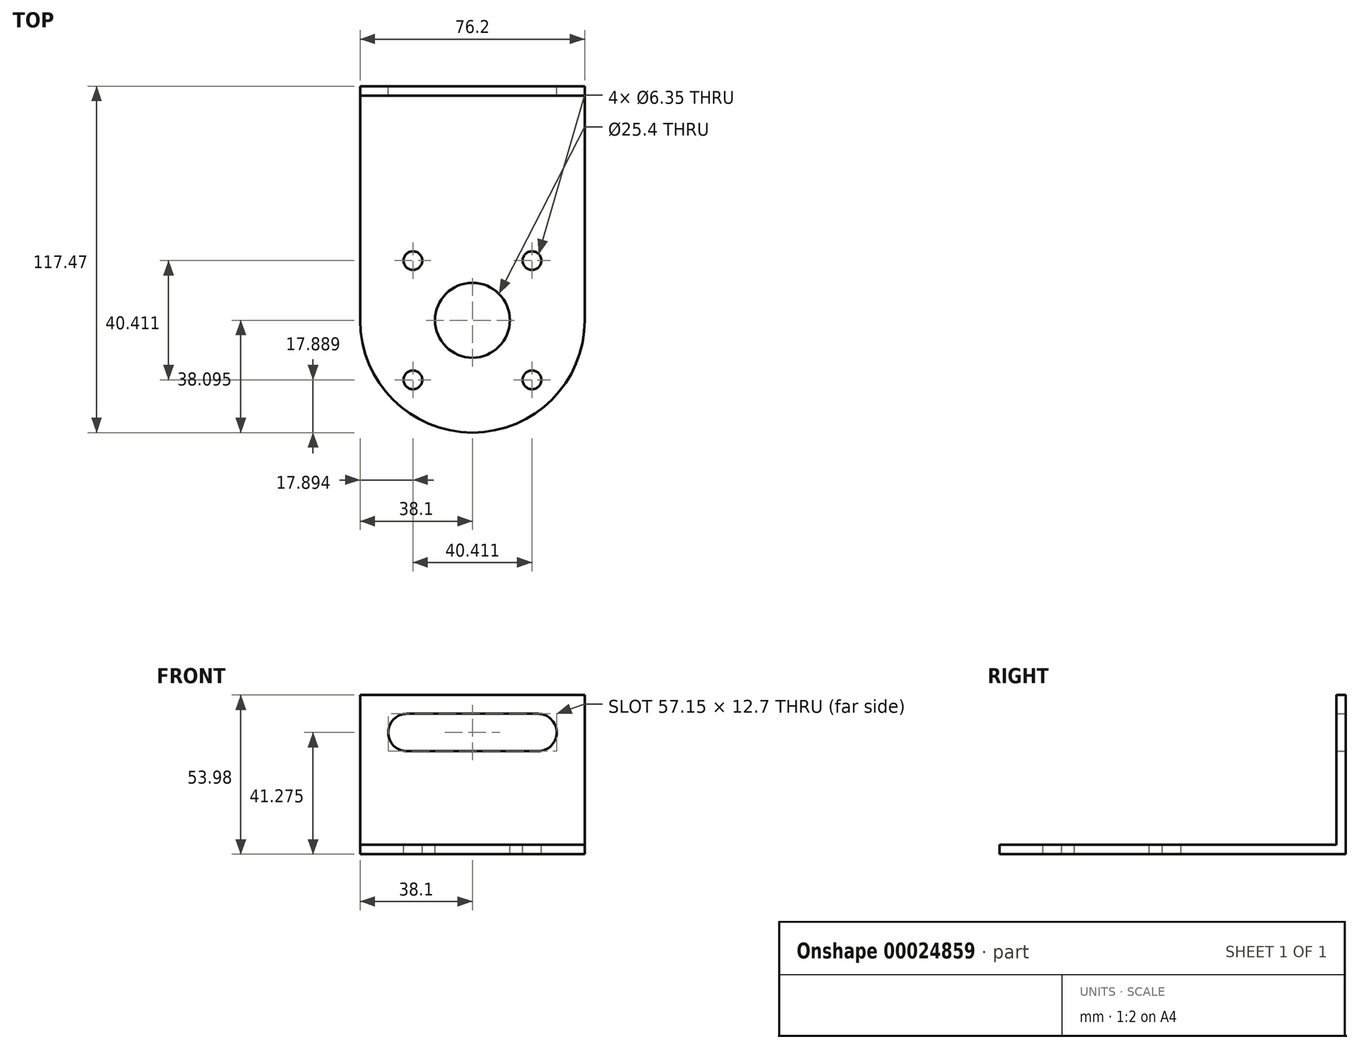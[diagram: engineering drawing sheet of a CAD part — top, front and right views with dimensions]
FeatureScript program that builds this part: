
annotation { "Feature Type Name" : "Feature", "Feature Type Description" : "" }
export const myFeature = defineFeature(function(context is Context, id is Id, definition is map)
    precondition{}
    {
        {
            var Q0;
            Q0=qCreatedBy(makeId("Front.planeOp"),FACE);
            var sketch = newSketch(context, id + "F0", { "sketchPlane" : qUnion([Q0])});
            skLineSegment(sketch, "E0.bottom", {"start": v(0, 0) * mm, "end": v(76.2, 0) * mm});
            skLineSegment(sketch, "E0.top", {"start": v(0, 53.97) * mm, "end": v(76.2, 53.97) * mm});
            skLineSegment(sketch, "E0.left", {"start": v(0, 0) * mm, "end": v(0, 53.97) * mm});
            skLineSegment(sketch, "E0.right", {"start": v(76.2, 0) * mm, "end": v(76.2, 53.97) * mm});
            skLineSegment(sketch, "E1", {"start": v(0, 41.27) * mm, "end": v(76.2, 41.27) * mm, "construction": true});
            skLineSegment(sketch, "E2", {"start": v(60.32, 53.97) * mm, "end": v(60.32, 0) * mm, "construction": true});
            skLineSegment(sketch, "E3", {"start": v(15.87, 53.97) * mm, "end": v(15.88, 0) * mm, "construction": true});
            skArc(sketch, "E4", {"start": v(15.87, 47.62) * mm, "mid": v(9.52, 41.27) * mm, "end": v(15.87, 34.92) * mm});
            skArc(sketch, "E5", {"start": v(60.32, 34.92) * mm, "mid": v(66.67, 41.27) * mm, "end": v(60.32, 47.62) * mm});
            skLineSegment(sketch, "E6", {"start": v(15.87, 47.62) * mm, "end": v(60.32, 47.62) * mm});
            skLineSegment(sketch, "E7", {"start": v(15.87, 34.92) * mm, "end": v(60.32, 34.92) * mm});
            skSolve(sketch);
        }
        {
            var Q0;
            Q0=makeQuery(id+"F0.imprint","IMPRINT",FACE,{"disambiguationData":[TD([[makeQuery(id+"F0.imprint","IMPRINT",EDGE,{"derivedFrom":sQuery(id+"F0.wireOp",EDGE,"E0.bottom")}),1.0]])]});
            extrude(context, id + "F1", {"entities" : qUnion([Q0]), "depth" : 3.17 * mm});
        }
        {
            var Q0;
            Q0=makeQuery(id+"F1.opExtrude","CAP_FACE",FACE,{"disambiguationData":[OSD([sQuery(id+"F0.wireOp",EDGE,"E0.bottom"),sQuery(id+"F0.wireOp",EDGE,"E0.top"),sQuery(id+"F0.wireOp",EDGE,"E0.left"),sQuery(id+"F0.wireOp",EDGE,"E0.right"),sQuery(id+"F0.wireOp",EDGE,"E4"),sQuery(id+"F0.wireOp",EDGE,"E5"),sQuery(id+"F0.wireOp",EDGE,"E6"),sQuery(id+"F0.wireOp",EDGE,"E7")])],"isStart":false});
            var sketch = newSketch(context, id + "F2", { "sketchPlane" : qUnion([Q0])});
            skLineSegment(sketch, "E8", {"start": v(0, 3.18) * mm, "end": v(76.2, 3.18) * mm});
            skSolve(sketch);
        }
        {
            var Q0;
            {var subQ1=sQuery(id+"F2.wireOp",EDGE,"E8");Q0=makeQuery(id+"F2.imprint","IMPRINT",FACE,{"disambiguationData":[TD([[makeQuery(id+"F2.imprint","IMPRINT",EDGE,{"derivedFrom":subQ1}),-1.0]])]});}
            extrude(context, id + "F3", {"entities" : qUnion([Q0]), "operationType" : NewBodyOperationType.ADD, "depth" : 76.2 * mm});
        }
        {
            var Q0;
            Q0=makeQuery(id+"F3.opExtrude","SWEPT_FACE",FACE,{"disambiguationData":[OSD([sQuery(id+"F2.wireOp",EDGE,"E8")])]});
            var sketch = newSketch(context, id + "F4", { "sketchPlane" : qUnion([Q0])});
            skArc(sketch, "E9", {"start": v(0, -79.38) * mm, "mid": v(38.1, -117.47) * mm, "end": v(76.2, -79.38) * mm});
            skLineSegment(sketch, "E10", {"start": v(0, -79.38) * mm, "end": v(76.2, -79.38) * mm, "construction": true});
            skSolve(sketch);
        }
        {
            var Q0;
            Q0=makeQuery(id+"F4.imprint","IMPRINT",FACE,{"disambiguationData":[TD([[makeQuery(id+"F4.imprint","IMPRINT",EDGE,{"derivedFrom":sQuery(id+"F4.wireOp",EDGE,"E9")}),1.0]])]});
            extrude(context, id + "F5", {"entities" : qUnion([Q0]), "operationType" : NewBodyOperationType.ADD, "oppositeDirection" : true, "depth" : 3.17 * mm});
        }
        {
            var Q0;
            {var subQ0=sQuery(id+"F2.wireOp",EDGE,"E8");Q0=makeQuery(id+"F5.boolean.opBoolean","MERGE",FACE,{"derivedFrom":[makeQuery(id+"F3.opExtrude","SWEPT_FACE",FACE,{"disambiguationData":[OSD([subQ0])]}),makeQuery(id+"F5.opExtrude","CAP_FACE",FACE,{"disambiguationData":[OSD([subQ0,sQuery(id+"F4.wireOp",EDGE,"E9")])],"isStart":true})]});}
            var sketch = newSketch(context, id + "F6", { "sketchPlane" : qUnion([Q0])});
            skLineSegment(sketch, "E11", {"start": v(76.2, -79.38) * mm, "end": v(0, -79.38) * mm, "construction": true});
            skLineSegment(sketch, "E12", {"start": v(38.1, -79.38) * mm, "end": v(38.1, -145.79) * mm, "construction": true});
            skCircle(sketch, "E13", {"center": v(38.1, -79.38) * mm, "radius": 12.7 * mm});
            skCircle(sketch, "E14", {"center": v(38.1, -79.38) * mm, "radius": 28.58 * mm, "construction": true});
            skLineSegment(sketch, "E15", {"start": v(38.1, -79.38) * mm, "end": v(87.4, -128.68) * mm, "construction": true});
            skCircle(sketch, "E16", {"center": v(58.3, -99.58) * mm, "radius": 3.18 * mm});
            skCircle(sketch, "E17.1.0", {"center": v(58.3, -59.17) * mm, "radius": 3.18 * mm});
            skCircle(sketch, "E17.2.0", {"center": v(17.9, -59.17) * mm, "radius": 3.18 * mm});
            skCircle(sketch, "E17.3.0", {"center": v(17.9, -99.58) * mm, "radius": 3.18 * mm});
            skSolve(sketch);
        }
        {
            var Q0;
            Q0=makeQuery(id+"F6.imprint","IMPRINT",FACE,{"disambiguationData":[TD([[makeQuery(id+"F6.imprint","IMPRINT",EDGE,{"derivedFrom":sQuery(id+"F6.wireOp",EDGE,"E16")}),1.0]])]});
            var Q1;
            Q1=makeQuery(id+"F6.imprint","IMPRINT",FACE,{"disambiguationData":[TD([[makeQuery(id+"F6.imprint","IMPRINT",EDGE,{"derivedFrom":sQuery(id+"F6.wireOp",EDGE,"E13")}),1.0]])]});
            var Q2;
            Q2=makeQuery(id+"F6.imprint","IMPRINT",FACE,{"disambiguationData":[TD([[makeQuery(id+"F6.imprint","IMPRINT",EDGE,{"derivedFrom":sQuery(id+"F6.wireOp",EDGE,"E17.2.0")}),1.0]])]});
            var Q3;
            Q3=makeQuery(id+"F6.imprint","IMPRINT",FACE,{"disambiguationData":[TD([[makeQuery(id+"F6.imprint","IMPRINT",EDGE,{"derivedFrom":sQuery(id+"F6.wireOp",EDGE,"E17.1.0")}),1.0]])]});
            var Q4;
            Q4=makeQuery(id+"F6.imprint","IMPRINT",FACE,{"disambiguationData":[TD([[makeQuery(id+"F6.imprint","IMPRINT",EDGE,{"derivedFrom":sQuery(id+"F6.wireOp",EDGE,"E17.3.0")}),1.0]])]});
            extrude(context, id + "F7", {"entities" : qUnion([Q0, Q1, Q2, Q3, Q4]), "operationType" : NewBodyOperationType.REMOVE, "oppositeDirection" : true, "depth" : 25.4 * mm});
        }
    });
